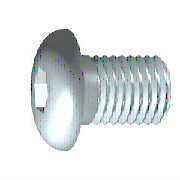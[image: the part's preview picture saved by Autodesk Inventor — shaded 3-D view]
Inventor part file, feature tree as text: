
AUTODESK INVENTOR PART (.ipt)
format: ipt  version: 2013 (Build 170138000, 138)  size: 186,368 bytes
history: native  units: mm (DEFAULTED — no unit token found)
features: sketch x2, extrude x1, plane x1
ambient origin geometry x7: Origin, YZ Plane, XY Plane, X Axis, Y Axis, Z Axis, Center Point
bodies: Solid1 (feature_tree), Body (feature_tree)
feature tree (4):
  extrude  "Slot"  Depth=0.49076mm
  plane  "Work Plane1"
  sketch  "Sketch1"  dims[d0=28.4mm d1=0.49076mm]
  sketch  "Sketch2"  dims[d2=2.75mm d3=1.56mm d4=60.0deg d5=5.0mm d6=5.0mm d7=3.464102mm d8=9.5mm d10=90.0deg d11=10.0mm d9=0.0mm d12=28.4mm d13=0.0mm d14=0.49076mm d15=0.49076mm d16=2.375mm d17=0.0mm d18=0.0mm d19=30.0mm d27=45.0deg d28=0.2mm d29=0.2mm]
